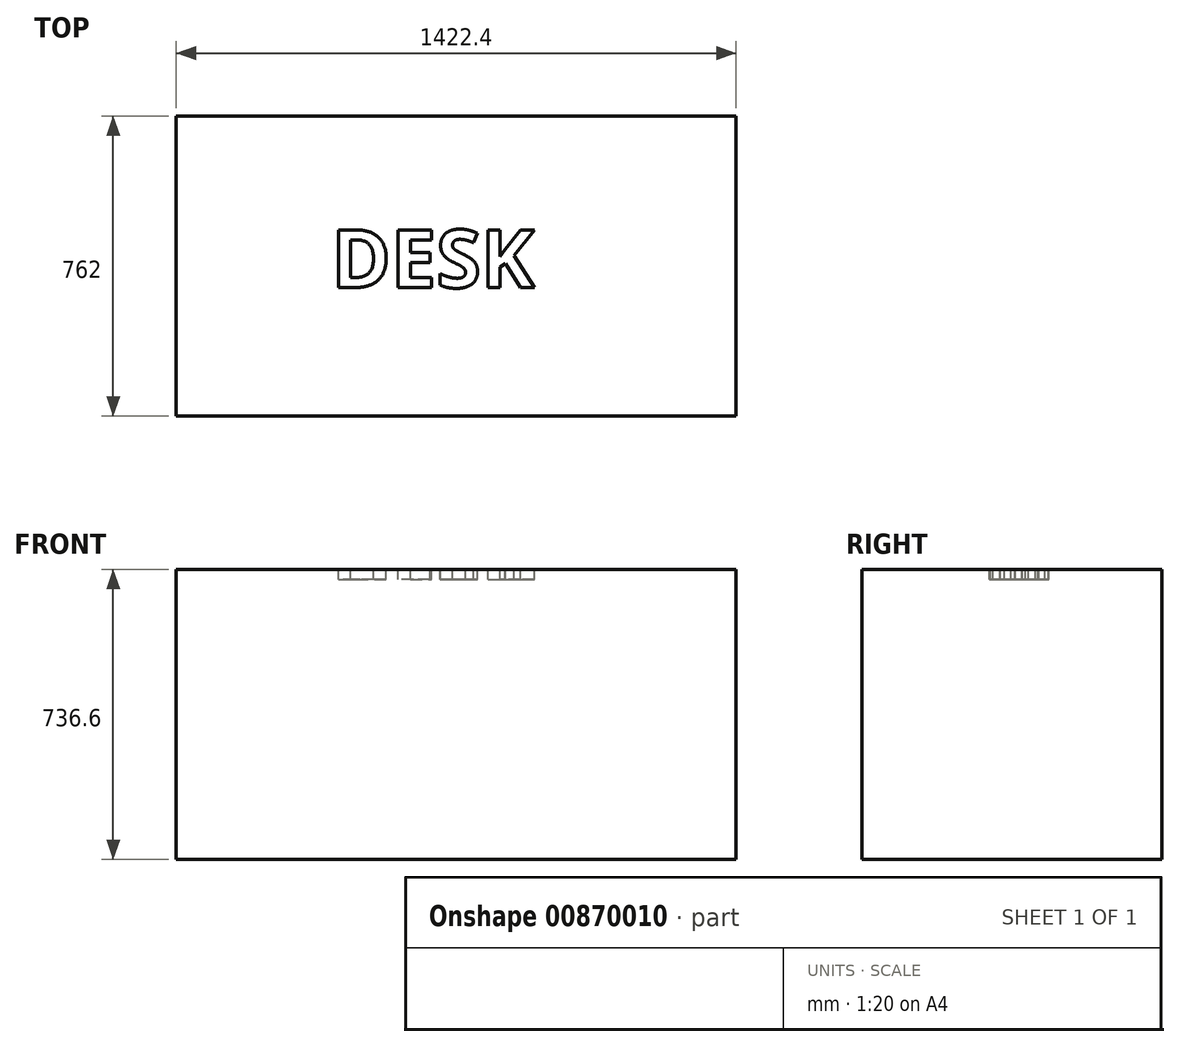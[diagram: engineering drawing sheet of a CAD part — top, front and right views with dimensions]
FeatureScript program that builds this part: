
annotation { "Feature Type Name" : "Feature", "Feature Type Description" : "" }
export const myFeature = defineFeature(function(context is Context, id is Id, definition is map)
    precondition{}
    {
        {
            var Q0;
            Q0=qCreatedBy(makeId("Top.planeOp"),FACE);
            var sketch = newSketch(context, id + "F0", { "sketchPlane" : qUnion([Q0])});
            skLineSegment(sketch, "E0.bottom", {"start": v(0, 0) * mm, "end": v(1422.4, 0) * mm});
            skLineSegment(sketch, "E0.top", {"start": v(0, 762) * mm, "end": v(1422.4, 762) * mm});
            skLineSegment(sketch, "E0.left", {"start": v(0, 0) * mm, "end": v(0, 762) * mm});
            skLineSegment(sketch, "E0.right", {"start": v(1422.4, 0) * mm, "end": v(1422.4, 762) * mm});
            skSolve(sketch);
        }
        {
            var Q0;
            Q0 = qSketchRegion(id + "F0", true);
            extrude(context, id + "F1", {"entities" : qUnion([Q0]), "depth" : 736.6 * mm, "offsetDistance" : 25.4 * mm});
        }
        {
            var Q0;
            Q0=makeQuery(id+"F1.opExtrude","CAP_FACE",FACE,{"disambiguationData":[OSD([sQuery(id+"F0.wireOp",EDGE,"E0.bottom"),sQuery(id+"F0.wireOp",EDGE,"E0.top"),sQuery(id+"F0.wireOp",EDGE,"E0.left"),sQuery(id+"F0.wireOp",EDGE,"E0.right")])],"isStart":false});
            var sketch = newSketch(context, id + "F2", { "sketchPlane" : qUnion([Q0])});
            skText(sketch, "E1", { "text": "DESK", "fontName": "OpenSans-Bold.ttf"});
            const initialGuessF2  = {"E1": [0.39347, 0.32615, 1, 0, 0.14788]};
            skSetInitialGuess(sketch, initialGuessF2);
            skSolve(sketch);
        }
        {
            var Q0;
            Q0 = qSketchRegion(id + "F2", true);
            extrude(context, id + "F3", {"entities" : qUnion([Q0]), "operationType" : NewBodyOperationType.REMOVE, "oppositeDirection" : true, "depth" : 25.4 * mm, "offsetDistance" : 25.4 * mm});
        }
    });
